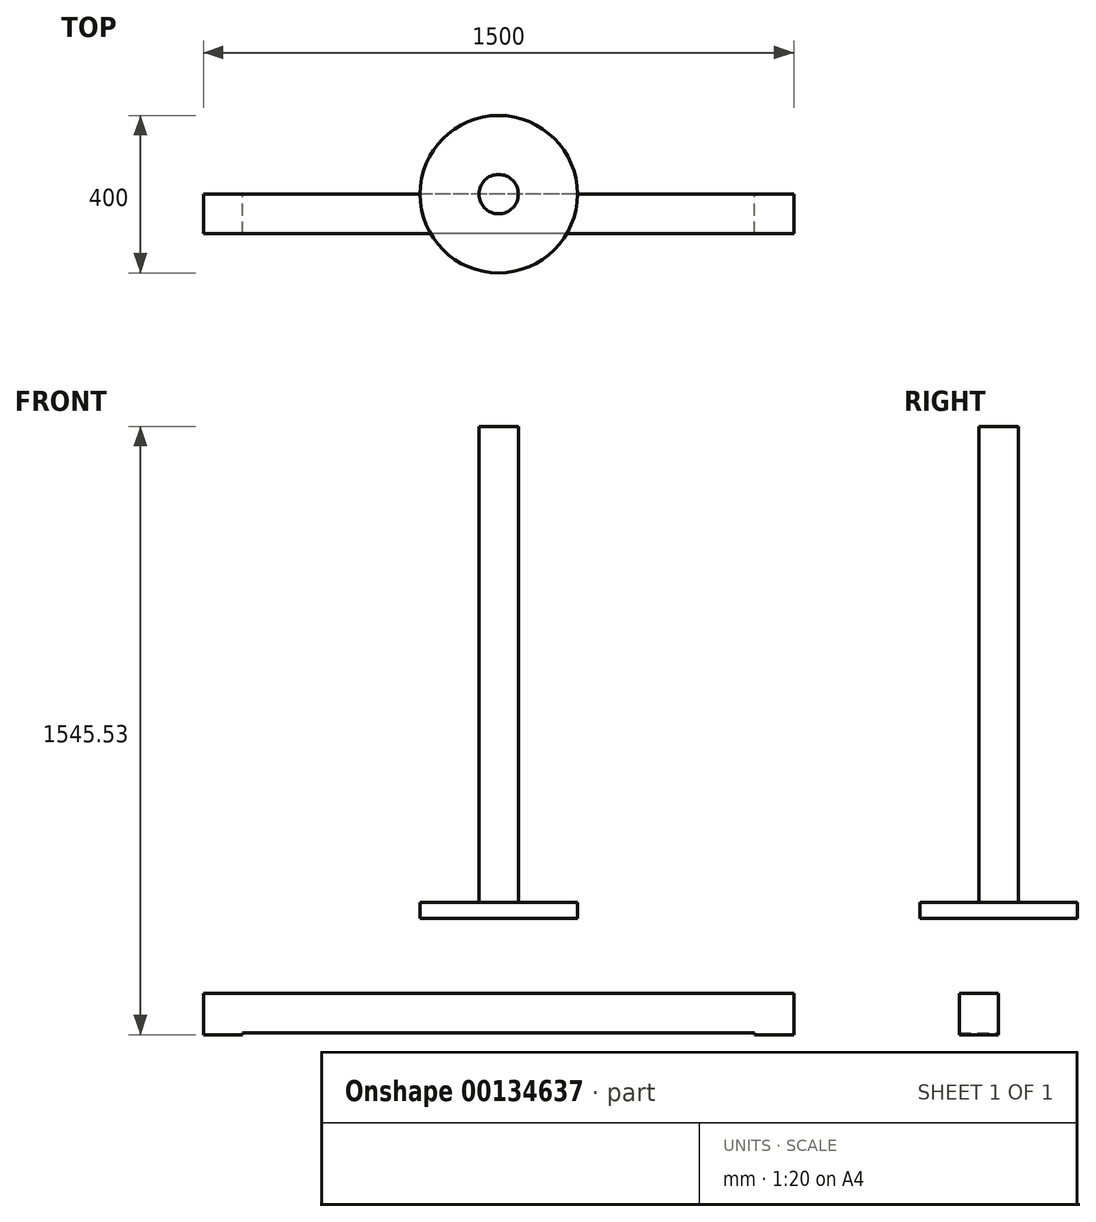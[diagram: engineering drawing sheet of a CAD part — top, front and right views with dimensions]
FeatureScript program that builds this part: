
annotation { "Feature Type Name" : "Feature", "Feature Type Description" : "" }
export const myFeature = defineFeature(function(context is Context, id is Id, definition is map)
    precondition{}
    {
        {
            var Q0;
            Q0=qCreatedBy(makeId("Top.planeOp"),FACE);
            var sketch = newSketch(context, id + "F0", { "sketchPlane" : qUnion([Q0])});
            skCircle(sketch, "E0", {"center": v(0, 0) * mm, "radius": 200 * mm});
            skCircle(sketch, "E1", {"center": v(0, 0) * mm, "radius": 50 * mm});
            skSolve(sketch);
        }
        {
            var Q0;
            Q0=makeQuery(id+"F0.imprint","IMPRINT",FACE,{"disambiguationData":[TD([[makeQuery(id+"F0.imprint","IMPRINT",EDGE,{"derivedFrom":sQuery(id+"F0.wireOp",EDGE,"E0")}),1.0]])]});
            var Q1;
            Q1=makeQuery(id+"F0.imprint","IMPRINT",FACE,{"disambiguationData":[TD([[makeQuery(id+"F0.imprint","IMPRINT",EDGE,{"derivedFrom":sQuery(id+"F0.wireOp",EDGE,"E1")}),1.0]])]});
            extrude(context, id + "F1", {"entities" : qUnion([Q0, Q1]), "depth" : 40 * mm});
        }
        {
            var Q0;
            Q0=makeQuery(id+"F0.imprint","IMPRINT",FACE,{"disambiguationData":[TD([[makeQuery(id+"F0.imprint","IMPRINT",EDGE,{"derivedFrom":sQuery(id+"F0.wireOp",EDGE,"E1")}),1.0]])]});
            extrude(context, id + "F2", {"entities" : qUnion([Q0]), "operationType" : NewBodyOperationType.ADD, "depth" : 1250 * mm});
        }
        {
            var Q0;
            Q0=qCreatedBy(makeId("Front.planeOp"),FACE);
            var sketch = newSketch(context, id + "F3", { "sketchPlane" : qUnion([Q0])});
            skLineSegment(sketch, "E2.bottom", {"start": v(750, -190.53) * mm, "end": v(-750, -190.53) * mm});
            skLineSegment(sketch, "E2.top", {"start": v(750, -290.53) * mm, "end": v(-750, -290.53) * mm});
            skLineSegment(sketch, "E2.left", {"start": v(750, -190.53) * mm, "end": v(750, -290.53) * mm});
            skLineSegment(sketch, "E2.right", {"start": v(-750, -190.53) * mm, "end": v(-750, -290.53) * mm});
            skPoint(sketch, "E2.middle", {"position": v(0, -240.53) * mm});
            skSolve(sketch);
        }
        {
            var Q0;
            Q0=makeQuery(id+"F3.imprint","IMPRINT",FACE,{"disambiguationData":[TD([[makeQuery(id+"F3.imprint","IMPRINT",EDGE,{"derivedFrom":sQuery(id+"F3.wireOp",EDGE,"E2.bottom")}),1.0]])]});
            extrude(context, id + "F4", {"entities" : qUnion([Q0]), "depth" : 100 * mm});
        }
        {
            var Q0;
            Q0=makeQuery(id+"F4.opExtrude","SWEPT_FACE",FACE,{"disambiguationData":[OSD([sQuery(id+"F3.wireOp",EDGE,"E2.top")])]});
            var sketch = newSketch(context, id + "F5", { "sketchPlane" : qUnion([Q0])});
            skLineSegment(sketch, "E3.bottom", {"start": v(-750, 100) * mm, "end": v(-650, 100) * mm});
            skLineSegment(sketch, "E3.top", {"start": v(-750, 0) * mm, "end": v(-650, 0) * mm});
            skLineSegment(sketch, "E3.left", {"start": v(-750, 100) * mm, "end": v(-750, 0) * mm});
            skLineSegment(sketch, "E3.right", {"start": v(-650, 100) * mm, "end": v(-650, 0) * mm});
            skLineSegment(sketch, "E4.bottom", {"start": v(750, 100) * mm, "end": v(650, 100) * mm});
            skLineSegment(sketch, "E4.top", {"start": v(750, 0) * mm, "end": v(650, 0) * mm});
            skLineSegment(sketch, "E4.left", {"start": v(750, 100) * mm, "end": v(750, 0) * mm});
            skLineSegment(sketch, "E4.right", {"start": v(650, 100) * mm, "end": v(650, 0) * mm});
            skSolve(sketch);
        }
        {
            var Q0;
            Q0=makeQuery(id+"F5.imprint","IMPRINT",FACE,{"disambiguationData":[TD([[makeQuery(id+"F5.imprint","IMPRINT",EDGE,{"derivedFrom":sQuery(id+"F5.wireOp",EDGE,"E3.bottom")}),1.0]])]});
            var Q1;
            Q1=makeQuery(id+"F5.imprint","IMPRINT",FACE,{"disambiguationData":[TD([[makeQuery(id+"F5.imprint","IMPRINT",EDGE,{"derivedFrom":sQuery(id+"F5.wireOp",EDGE,"E4.bottom")}),1.0]])]});
            extrude(context, id + "F6", {"entities" : qUnion([Q0, Q1]), "operationType" : NewBodyOperationType.ADD, "depth" : 5 * mm});
        }
    });
